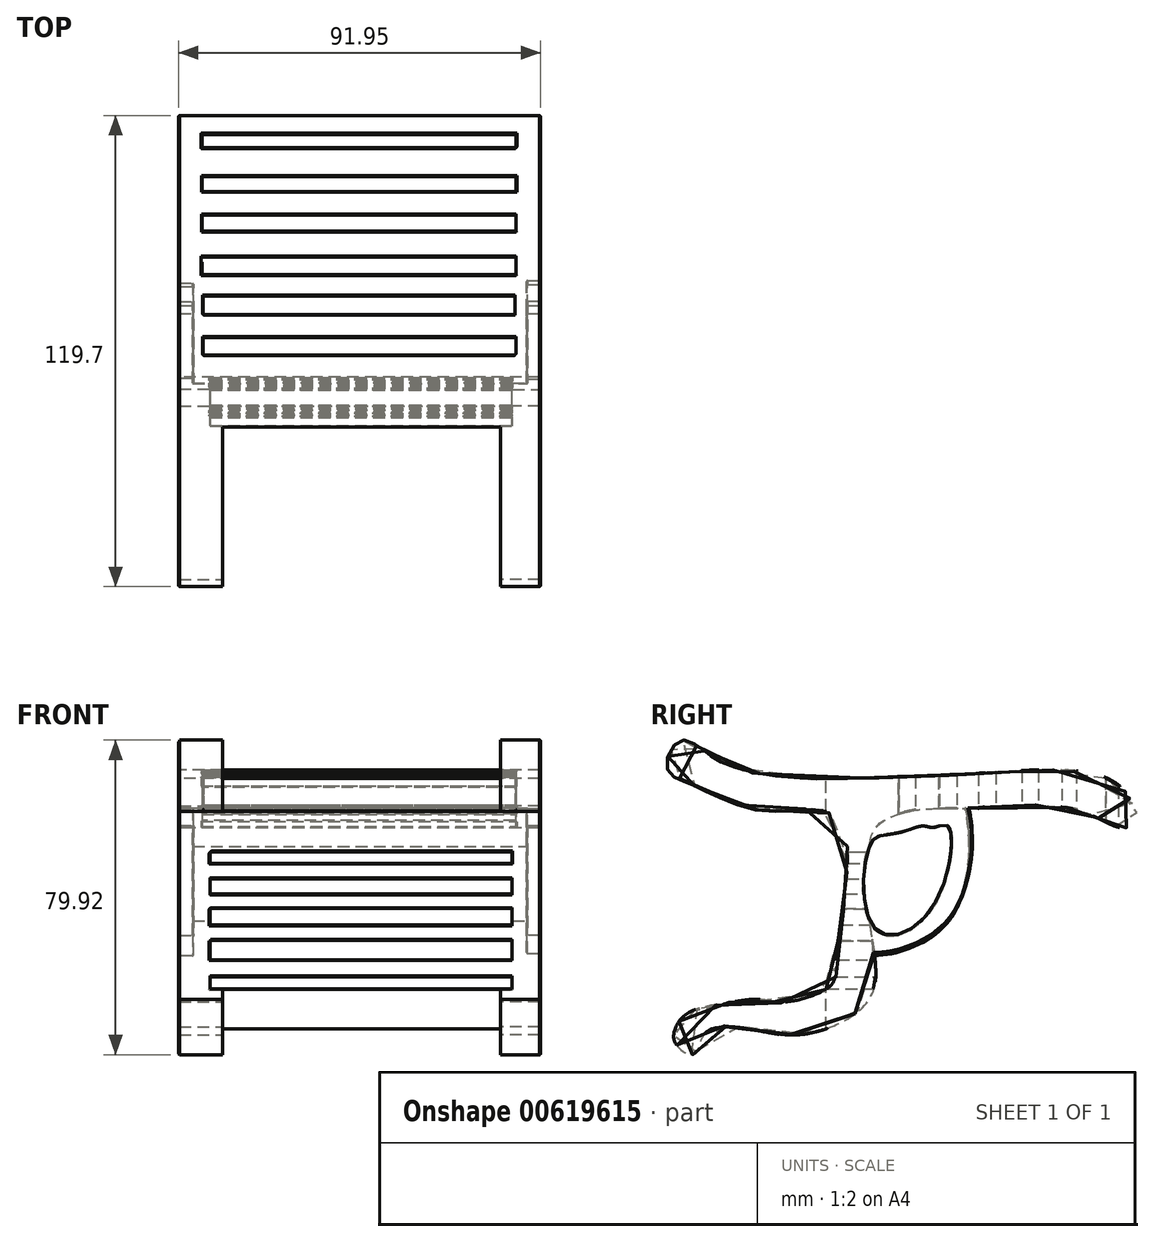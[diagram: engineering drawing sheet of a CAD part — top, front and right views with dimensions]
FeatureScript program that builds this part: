
annotation { "Feature Type Name" : "Feature", "Feature Type Description" : "" }
export const myFeature = defineFeature(function(context is Context, id is Id, definition is map)
    precondition{}
    {
        {
            var Q0;
            Q0=qCreatedBy(makeId("Right.planeOp"),FACE);
            var sketch = newSketch(context, id + "F0", { "sketchPlane" : qUnion([Q0])});
            skFitSpline(sketch, "E0", {"points": [v(46.73, 38) * mm, v(37.67, 44.46) * mm, v(9.54, 44.79) * mm, v(-13.1, 43.82) * mm, v(-44.46, 44.14) * mm, v(-59.01, 48.34) * mm, v(-62.9, 51.25) * mm, v(-68.07, 52.87) * mm, v(-71.3, 46.08) * mm, v(-67.42, 42.84) * mm, v(-61.6, 40.26) * mm, v(-46.4, 35.08) * mm, v(-31.2, 35.08) * mm, v(-26.03, 28.62) * mm, v(-26.35, 11.8) * mm, v(-27.97, 0) * mm, v(-28.94, -8.25) * mm, v(-33.47, -11.48) * mm, v(-41.55, -13.42) * mm, v(-48.02, -12.77) * mm, v(-54.49, -13.42) * mm, v(-64.83, -15.68) * mm, v(-68.71, -19.24) * mm, v(-69.04, -24.1) * mm, v(-64.19, -26.68) * mm, v(-61.92, -21.83) * mm, v(-53.2, -19.89) * mm, v(-40.26, -21.83) * mm, v(-27.65, -18.92) * mm, v(-18.92, -10.83) * mm, v(-19.56, 5.98) * mm, v(-19.89, 25.7) * mm, v(-17.3, 31.85) * mm, v(-7.28, 35.4) * mm, v(5.98, 35.73) * mm, v(32.82, 35.4) * mm, v(43.82, 30.88) * mm, v(48.02, 32.17) * mm, v(46.73, 38) * mm]});
            skSolve(sketch);
        }
        {
            var Q0;
            Q0=makeQuery(id+"F0.imprint","IMPRINT",FACE,{"disambiguationData":[TD([[makeQuery(id+"F0.imprint","IMPRINT",EDGE,{"derivedFrom":sQuery(id+"F0.wireOp",EDGE,"E0")}),1.0]])]});
            extrude(context, id + "F1", {"entities" : qUnion([Q0]), "oppositeDirection" : true, "depth" : 91.95 * mm, "offsetDistance" : 25.4 * mm});
        }
        {
            var Q0;
            Q0=qCreatedBy(makeId("Top.planeOp"),FACE);
            var sketch = newSketch(context, id + "F2", { "sketchPlane" : qUnion([Q0])});
            skLineSegment(sketch, "E1.bottom", {"start": v(-6.18, 43.47) * mm, "end": v(-85.94, 43.47) * mm});
            skLineSegment(sketch, "E1.top", {"start": v(-6.18, 40.12) * mm, "end": v(-85.94, 40.12) * mm});
            skLineSegment(sketch, "E1.left", {"start": v(-6.18, 43.47) * mm, "end": v(-6.18, 40.12) * mm});
            skLineSegment(sketch, "E1.right", {"start": v(-85.94, 43.47) * mm, "end": v(-85.94, 40.12) * mm});
            skLineSegment(sketch, "E2.bottom", {"start": v(-6.18, 32.82) * mm, "end": v(-85.94, 32.82) * mm});
            skLineSegment(sketch, "E2.top", {"start": v(-6.18, 29.04) * mm, "end": v(-85.94, 29.04) * mm});
            skLineSegment(sketch, "E2.left", {"start": v(-6.18, 32.82) * mm, "end": v(-6.18, 29.04) * mm});
            skLineSegment(sketch, "E2.right", {"start": v(-85.94, 32.82) * mm, "end": v(-85.94, 29.04) * mm});
            skLineSegment(sketch, "E3.bottom", {"start": v(-6.18, 23.06) * mm, "end": v(-85.94, 23.06) * mm});
            skLineSegment(sketch, "E3.top", {"start": v(-6.18, 18.94) * mm, "end": v(-85.94, 18.94) * mm});
            skLineSegment(sketch, "E3.left", {"start": v(-6.18, 23.06) * mm, "end": v(-6.18, 18.94) * mm});
            skLineSegment(sketch, "E3.right", {"start": v(-85.94, 23.06) * mm, "end": v(-85.94, 18.94) * mm});
            skLineSegment(sketch, "E4.bottom", {"start": v(-6.18, 12.38) * mm, "end": v(-85.94, 12.38) * mm});
            skLineSegment(sketch, "E4.top", {"start": v(-6.18, 7.9) * mm, "end": v(-85.94, 7.9) * mm});
            skLineSegment(sketch, "E4.left", {"start": v(-6.18, 12.38) * mm, "end": v(-6.18, 7.9) * mm});
            skLineSegment(sketch, "E4.right", {"start": v(-85.94, 12.38) * mm, "end": v(-85.94, 7.9) * mm});
            skLineSegment(sketch, "E5.left", {"start": v(-6.18, 0) * mm, "end": v(-6.18, -5.36) * mm});
            skLineSegment(sketch, "E5.right", {"start": v(-85.94, 0) * mm, "end": v(-85.94, -5.36) * mm});
            skSolve(sketch);
        }
        {
            var Q0;
            Q0 = qSketchRegion(id + "F2", true);
            extrude(context, id + "F3", {"entities" : qUnion([Q0]), "operationType" : NewBodyOperationType.REMOVE, "depth" : 122.68 * mm, "offsetDistance" : 25.4 * mm});
        }
        {
            var Q0;
            Q0=qCreatedBy(makeId("Top.planeOp"),FACE);
            var sketch = newSketch(context, id + "F4", { "sketchPlane" : qUnion([Q0])});
            skLineSegment(sketch, "E6.bottom", {"start": v(-10.2, -30.88) * mm, "end": v(-80.78, -30.88) * mm});
            skLineSegment(sketch, "E6.top", {"start": v(-10.2, -74.25) * mm, "end": v(-80.78, -74.25) * mm});
            skLineSegment(sketch, "E6.left", {"start": v(-10.2, -30.88) * mm, "end": v(-10.2, -74.25) * mm});
            skLineSegment(sketch, "E6.right", {"start": v(-80.78, -30.88) * mm, "end": v(-80.78, -74.25) * mm});
            skSolve(sketch);
        }
        {
            var Q0;
            Q0=makeQuery(id+"F4.imprint","IMPRINT",FACE,{"disambiguationData":[TD([[makeQuery(id+"F4.imprint","IMPRINT",EDGE,{"derivedFrom":sQuery(id+"F4.wireOp",EDGE,"E6.bottom")}),1.0]])]});
            extrude(context, id + "F5", {"entities" : qUnion([Q0]), "operationType" : NewBodyOperationType.REMOVE, "oppositeDirection" : true, "depth" : 64 * mm, "offsetDistance" : 25.4 * mm, "hasSecondDirection" : true, "secondDirectionOppositeDirection" : false, "secondDirectionDepth" : 97.28 * mm});
        }
        {
            var Q0;
            Q0=qCreatedBy(makeId("Front.planeOp"),FACE);
            var sketch = newSketch(context, id + "F6", { "sketchPlane" : qUnion([Q0])});
            skLineSegment(sketch, "E7.bottom", {"start": v(-7.26, 24.75) * mm, "end": v(-83.96, 24.75) * mm});
            skLineSegment(sketch, "E7.top", {"start": v(-7.26, 21.8) * mm, "end": v(-83.96, 21.8) * mm});
            skLineSegment(sketch, "E7.left", {"start": v(-7.26, 24.75) * mm, "end": v(-7.26, 21.8) * mm});
            skLineSegment(sketch, "E7.right", {"start": v(-83.96, 24.75) * mm, "end": v(-83.96, 21.8) * mm});
            skLineSegment(sketch, "E8.bottom", {"start": v(-7.26, 17.89) * mm, "end": v(-83.96, 17.89) * mm});
            skLineSegment(sketch, "E8.top", {"start": v(-7.26, 13.97) * mm, "end": v(-83.96, 13.97) * mm});
            skLineSegment(sketch, "E8.left", {"start": v(-7.26, 17.89) * mm, "end": v(-7.26, 13.97) * mm});
            skLineSegment(sketch, "E8.right", {"start": v(-83.96, 17.89) * mm, "end": v(-83.96, 13.97) * mm});
            skLineSegment(sketch, "E9.bottom", {"start": v(-7.26, 10.3) * mm, "end": v(-83.96, 10.3) * mm});
            skLineSegment(sketch, "E9.top", {"start": v(-7.26, 6.13) * mm, "end": v(-83.96, 6.13) * mm});
            skLineSegment(sketch, "E9.left", {"start": v(-7.26, 10.3) * mm, "end": v(-7.26, 6.13) * mm});
            skLineSegment(sketch, "E9.right", {"start": v(-83.96, 10.3) * mm, "end": v(-83.96, 6.13) * mm});
            skLineSegment(sketch, "E10.bottom", {"start": v(-7.26, 2.2) * mm, "end": v(-83.96, 2.2) * mm});
            skLineSegment(sketch, "E10.top", {"start": v(-7.26, -2.7) * mm, "end": v(-83.96, -2.7) * mm});
            skLineSegment(sketch, "E10.left", {"start": v(-7.26, 2.2) * mm, "end": v(-7.26, -2.7) * mm});
            skLineSegment(sketch, "E10.right", {"start": v(-83.96, 2.2) * mm, "end": v(-83.96, -2.7) * mm});
            skLineSegment(sketch, "E11.bottom", {"start": v(-7.26, -7.1) * mm, "end": v(-83.96, -7.1) * mm});
            skLineSegment(sketch, "E11.top", {"start": v(-7.26, -10.05) * mm, "end": v(-83.96, -10.05) * mm});
            skLineSegment(sketch, "E11.left", {"start": v(-7.26, -7.1) * mm, "end": v(-7.26, -10.05) * mm});
            skLineSegment(sketch, "E11.right", {"start": v(-83.96, -7.1) * mm, "end": v(-83.96, -10.05) * mm});
            skSolve(sketch);
        }
        {
            var Q0;
            Q0=makeQuery(id+"F6.imprint","IMPRINT",FACE,{"disambiguationData":[TD([[makeQuery(id+"F6.imprint","IMPRINT",EDGE,{"derivedFrom":sQuery(id+"F6.wireOp",EDGE,"E8.bottom")}),1.0]])]});
            var Q1;
            Q1=makeQuery(id+"F6.imprint","IMPRINT",FACE,{"disambiguationData":[TD([[makeQuery(id+"F6.imprint","IMPRINT",EDGE,{"derivedFrom":sQuery(id+"F6.wireOp",EDGE,"E9.bottom")}),1.0]])]});
            var Q2;
            Q2=makeQuery(id+"F6.imprint","IMPRINT",FACE,{"disambiguationData":[TD([[makeQuery(id+"F6.imprint","IMPRINT",EDGE,{"derivedFrom":sQuery(id+"F6.wireOp",EDGE,"E10.bottom")}),1.0]])]});
            var Q3;
            Q3=makeQuery(id+"F6.imprint","IMPRINT",FACE,{"disambiguationData":[TD([[makeQuery(id+"F6.imprint","IMPRINT",EDGE,{"derivedFrom":sQuery(id+"F6.wireOp",EDGE,"E11.bottom")}),1.0]])]});
            var Q4;
            Q4=makeQuery(id+"F6.imprint","IMPRINT",FACE,{"disambiguationData":[TD([[makeQuery(id+"F6.imprint","IMPRINT",EDGE,{"derivedFrom":sQuery(id+"F6.wireOp",EDGE,"E7.bottom")}),1.0]])]});
            extrude(context, id + "F7", {"entities" : qUnion([Q0, Q1, Q2, Q3, Q4]), "operationType" : NewBodyOperationType.REMOVE, "depth" : 131.83 * mm, "offsetDistance" : 25.4 * mm});
        }
        {
            var Q0;
            Q0=qCreatedBy(makeId("Top.planeOp"),FACE);
            var sketch = newSketch(context, id + "F8", { "sketchPlane" : qUnion([Q0])});
            skLineSegment(sketch, "E12.bottom", {"start": v(-85.68, 2.45) * mm, "end": v(-6.53, 2.45) * mm});
            skLineSegment(sketch, "E12.top", {"start": v(-85.68, -2.2) * mm, "end": v(-6.53, -2.2) * mm});
            skLineSegment(sketch, "E12.left", {"start": v(-85.68, 2.45) * mm, "end": v(-85.68, -2.2) * mm});
            skLineSegment(sketch, "E12.right", {"start": v(-6.53, 2.45) * mm, "end": v(-6.53, -2.2) * mm});
            skLineSegment(sketch, "E13.bottom", {"start": v(-85.68, -8.09) * mm, "end": v(-6.28, -8.09) * mm});
            skLineSegment(sketch, "E13.top", {"start": v(-85.68, -12.5) * mm, "end": v(-6.28, -12.5) * mm});
            skLineSegment(sketch, "E13.left", {"start": v(-85.68, -8.09) * mm, "end": v(-85.68, -12.5) * mm});
            skLineSegment(sketch, "E13.right", {"start": v(-6.28, -8.09) * mm, "end": v(-6.28, -12.5) * mm});
            skSolve(sketch);
        }
        {
            var Q0;
            Q0=makeQuery(id+"F8.imprint","IMPRINT",FACE,{"disambiguationData":[TD([[makeQuery(id+"F8.imprint","IMPRINT",EDGE,{"derivedFrom":sQuery(id+"F8.wireOp",EDGE,"E13.bottom")}),-1.0]])]});
            var Q1;
            Q1=makeQuery(id+"F8.imprint","IMPRINT",FACE,{"disambiguationData":[TD([[makeQuery(id+"F8.imprint","IMPRINT",EDGE,{"derivedFrom":sQuery(id+"F8.wireOp",EDGE,"E12.bottom")}),-1.0]])]});
            extrude(context, id + "F9", {"entities" : qUnion([Q0, Q1]), "operationType" : NewBodyOperationType.REMOVE, "depth" : 137.92 * mm, "offsetDistance" : 25.4 * mm});
        }
        {
            var Q0;
            Q0=qCreatedBy(makeId("Right.planeOp"),FACE);
            var sketch = newSketch(context, id + "F10", { "sketchPlane" : qUnion([Q0])});
            skFitSpline(sketch, "E14", {"points": [v(3.68, 39.62) * mm, v(0, 7.15) * mm, v(-23.77, 0) * mm, v(-24.33, 3.77) * mm, v(-24.45, 7.59) * mm, v(-24.54, 14.74) * mm, v(-23.4, 26.35) * mm, v(-21.86, 33.21) * mm, v(-13.38, 37.47) * mm, v(-2.7, 40.33) * mm, v(3.68, 39.62) * mm]});
            skSolve(sketch);
        }
        {
            var Q0;
            Q0=qCreatedBy(makeId("Right.planeOp"),FACE);
            cPlane(context, id + "F11", {"entities" : qUnion([Q0]), "cplaneType" : CPlaneType.OFFSET, "offset" : 91.95 * mm, "oppositeDirection" : true, "width" : 152.4 * mm, "height" : 152.4 * mm});
        }
        {
            var Q0;
            Q0=qCreatedBy(id+"F11.planeOp",FACE);
            var sketch = newSketch(context, id + "F12", { "sketchPlane" : qUnion([Q0])});
            skFitSpline(sketch, "E15", {"points": [v(3.68, 39.33) * mm, v(0, 6.74) * mm, v(-25, 0) * mm, v(-24.26, 9.43) * mm, v(-24.26, 17.28) * mm, v(-23.77, 28.06) * mm, v(-21.07, 34.18) * mm, v(-15.2, 37.86) * mm, v(0, 41.78) * mm, v(3.68, 39.33) * mm]});
            skSolve(sketch);
        }
        {
            var Q0;
            Q0=makeQuery(id+"F12.imprint","IMPRINT",FACE,{"disambiguationData":[TD([[makeQuery(id+"F12.imprint","IMPRINT",EDGE,{"derivedFrom":sQuery(id+"F12.wireOp",EDGE,"E15")}),-1.0]])]});
            extrude(context, id + "F13", {"entities" : qUnion([Q0]), "operationType" : NewBodyOperationType.ADD, "depth" : 3.8 * mm, "offsetDistance" : 25.4 * mm});
        }
        {
            var Q0;
            Q0=makeQuery(id+"F10.imprint","IMPRINT",FACE,{"disambiguationData":[TD([[makeQuery(id+"F10.imprint","IMPRINT",EDGE,{"derivedFrom":sQuery(id+"F10.wireOp",EDGE,"E14")}),-1.0]])]});
            extrude(context, id + "F14", {"entities" : qUnion([Q0]), "operationType" : NewBodyOperationType.ADD, "oppositeDirection" : true, "depth" : 3.56 * mm, "offsetDistance" : 25.4 * mm});
        }
        {
            var Q0;
            Q0=qCreatedBy(makeId("Right.planeOp"),FACE);
            var sketch = newSketch(context, id + "F15", { "sketchPlane" : qUnion([Q0])});
            skFitSpline(sketch, "E16", {"points": [v(0, 31.4) * mm, v(-4.05, 10.3) * mm, v(-18.34, 5.12) * mm, v(-19.58, 26.66) * mm, v(-15.73, 29.03) * mm, v(-10.4, 30.08) * mm, v(-6.14, 31.28) * mm, v(-3.42, 30.9) * mm, v(0, 31.4) * mm]});
            skFitSpline(sketch, "E17", {"points": [v(-6.14, 31.28) * mm, v(0, 31.4) * mm], "startDerivative": vector(6.14, 0.12) * mm, "endDerivative": vector(6.14, 0.12) * mm});
            skSolve(sketch);
        }
        {
            var Q0;
            {var subQ0=sQuery(id+"F15.wireOp",EDGE,"E17");var subQ1=sQuery(id+"F15.wireOp",EDGE,"E16");var subQ2=makeQuery(id+"F15.imprint","INTERSECT",VERTEX,{"disambiguationData":[OD(0.0)],"derivedFrom":[subQ1,subQ0]});Q0=makeQuery(id+"F15.imprint","IMPRINT",FACE,{"disambiguationData":[TD([[makeQuery(id+"F15.imprint","IMPRINT",EDGE,{"disambiguationData":[TD([[subQ2,1.0]])],"derivedFrom":subQ1}),-1.0]])]});}
            extrude(context, id + "F16", {"entities" : qUnion([Q0]), "operationType" : NewBodyOperationType.REMOVE, "oppositeDirection" : true, "depth" : 179.58 * mm, "offsetDistance" : 25.4 * mm});
        }
        {
            var Q0;
            Q0=makeQuery(id+"F1.opExtrude","CAP_EDGE",EDGE,{"disambiguationData":[OSD([sQuery(id+"F0.wireOp",EDGE,"E0")])],"isStart":true});
            var Q1;
            Q1=makeQuery(id+"F7.boolean.opBoolean","INTERSECT",EDGE,{"disambiguationData":[OD(1.0)],"derivedFrom":[makeQuery(id+"F1.opExtrude","SWEPT_FACE",FACE,{"disambiguationData":[OSD([sQuery(id+"F0.wireOp",EDGE,"E0")])]}),makeQuery(id+"F7.opExtrude","SWEPT_FACE",FACE,{"disambiguationData":[OSD([sQuery(id+"F6.wireOp",EDGE,"E11.top")])]})]});
            var Q2;
            Q2=makeQuery(id+"F7.boolean.opBoolean","INTERSECT",EDGE,{"disambiguationData":[OD(1.0)],"derivedFrom":[makeQuery(id+"F1.opExtrude","SWEPT_FACE",FACE,{"disambiguationData":[OSD([sQuery(id+"F0.wireOp",EDGE,"E0")])]}),makeQuery(id+"F7.opExtrude","SWEPT_FACE",FACE,{"disambiguationData":[OSD([sQuery(id+"F6.wireOp",EDGE,"E11.bottom")])]})]});
            var Q3;
            Q3=makeQuery(id+"F7.boolean.opBoolean","INTERSECT",EDGE,{"disambiguationData":[OD(1.0)],"derivedFrom":[makeQuery(id+"F1.opExtrude","SWEPT_FACE",FACE,{"disambiguationData":[OSD([sQuery(id+"F0.wireOp",EDGE,"E0")])]}),makeQuery(id+"F7.opExtrude","SWEPT_FACE",FACE,{"disambiguationData":[OSD([sQuery(id+"F6.wireOp",EDGE,"E10.top")])]})]});
            var Q4;
            Q4=makeQuery(id+"F7.boolean.opBoolean","INTERSECT",EDGE,{"disambiguationData":[OD(0.0)],"derivedFrom":[makeQuery(id+"F1.opExtrude","SWEPT_FACE",FACE,{"disambiguationData":[OSD([sQuery(id+"F0.wireOp",EDGE,"E0")])]}),makeQuery(id+"F7.opExtrude","SWEPT_FACE",FACE,{"disambiguationData":[OSD([sQuery(id+"F6.wireOp",EDGE,"E10.bottom")])]})]});
            var Q5;
            Q5=makeQuery(id+"F7.boolean.opBoolean","INTERSECT",EDGE,{"disambiguationData":[OD(1.0)],"derivedFrom":[makeQuery(id+"F1.opExtrude","SWEPT_FACE",FACE,{"disambiguationData":[OSD([sQuery(id+"F0.wireOp",EDGE,"E0")])]}),makeQuery(id+"F7.opExtrude","SWEPT_FACE",FACE,{"disambiguationData":[OSD([sQuery(id+"F6.wireOp",EDGE,"E10.bottom")])]})]});
            var Q6;
            Q6=makeQuery(id+"F7.boolean.opBoolean","INTERSECT",EDGE,{"disambiguationData":[OD(1.0)],"derivedFrom":[makeQuery(id+"F1.opExtrude","SWEPT_FACE",FACE,{"disambiguationData":[OSD([sQuery(id+"F0.wireOp",EDGE,"E0")])]}),makeQuery(id+"F7.opExtrude","SWEPT_FACE",FACE,{"disambiguationData":[OSD([sQuery(id+"F6.wireOp",EDGE,"E9.top")])]})]});
            var Q7;
            Q7=makeQuery(id+"F7.boolean.opBoolean","INTERSECT",EDGE,{"disambiguationData":[OD(0.0)],"derivedFrom":[makeQuery(id+"F1.opExtrude","SWEPT_FACE",FACE,{"disambiguationData":[OSD([sQuery(id+"F0.wireOp",EDGE,"E0")])]}),makeQuery(id+"F7.opExtrude","SWEPT_FACE",FACE,{"disambiguationData":[OSD([sQuery(id+"F6.wireOp",EDGE,"E9.bottom")])]})]});
            var Q8;
            Q8=makeQuery(id+"F16.boolean.opBoolean","INTERSECT",EDGE,{"derivedFrom":[makeQuery(id+"F7.boolean.opBoolean","COPY",FACE,{"derivedFrom":makeQuery(id+"F7.opExtrude","SWEPT_FACE",FACE,{"disambiguationData":[OSD([sQuery(id+"F6.wireOp",EDGE,"E9.bottom")])]})}),makeQuery(id+"F16.opExtrude","SWEPT_FACE",FACE,{"disambiguationData":[OSD([sQuery(id+"F15.wireOp",EDGE,"E16")])]})]});
            var Q9;
            Q9=makeQuery(id+"F16.boolean.opBoolean","INTERSECT",EDGE,{"derivedFrom":[makeQuery(id+"F7.boolean.opBoolean","COPY",FACE,{"derivedFrom":makeQuery(id+"F7.opExtrude","SWEPT_FACE",FACE,{"disambiguationData":[OSD([sQuery(id+"F6.wireOp",EDGE,"E8.top")])]})}),makeQuery(id+"F16.opExtrude","SWEPT_FACE",FACE,{"disambiguationData":[OSD([sQuery(id+"F15.wireOp",EDGE,"E16")])]})]});
            var Q10;
            Q10=makeQuery(id+"F16.boolean.opBoolean","INTERSECT",EDGE,{"derivedFrom":[makeQuery(id+"F7.boolean.opBoolean","COPY",FACE,{"derivedFrom":makeQuery(id+"F7.opExtrude","SWEPT_FACE",FACE,{"disambiguationData":[OSD([sQuery(id+"F6.wireOp",EDGE,"E8.bottom")])]})}),makeQuery(id+"F16.opExtrude","SWEPT_FACE",FACE,{"disambiguationData":[OSD([sQuery(id+"F15.wireOp",EDGE,"E16")])]})]});
            var Q11;
            Q11=makeQuery(id+"F16.boolean.opBoolean","INTERSECT",EDGE,{"derivedFrom":[makeQuery(id+"F7.boolean.opBoolean","COPY",FACE,{"derivedFrom":makeQuery(id+"F7.opExtrude","SWEPT_FACE",FACE,{"disambiguationData":[OSD([sQuery(id+"F6.wireOp",EDGE,"E7.top")])]})}),makeQuery(id+"F16.opExtrude","SWEPT_FACE",FACE,{"disambiguationData":[OSD([sQuery(id+"F15.wireOp",EDGE,"E16")])]})]});
            var Q12;
            Q12=makeQuery(id+"F16.boolean.opBoolean","INTERSECT",EDGE,{"derivedFrom":[makeQuery(id+"F7.boolean.opBoolean","COPY",FACE,{"derivedFrom":makeQuery(id+"F7.opExtrude","SWEPT_FACE",FACE,{"disambiguationData":[OSD([sQuery(id+"F6.wireOp",EDGE,"E7.bottom")])]})}),makeQuery(id+"F16.opExtrude","SWEPT_FACE",FACE,{"disambiguationData":[OSD([sQuery(id+"F15.wireOp",EDGE,"E16")])]})]});
            var Q13;
            Q13=makeQuery(id+"F9.boolean.opBoolean","INTERSECT",EDGE,{"disambiguationData":[OD(0.0)],"derivedFrom":[makeQuery(id+"F1.opExtrude","SWEPT_FACE",FACE,{"disambiguationData":[OSD([sQuery(id+"F0.wireOp",EDGE,"E0")])]}),makeQuery(id+"F9.opExtrude","SWEPT_FACE",FACE,{"disambiguationData":[OSD([sQuery(id+"F8.wireOp",EDGE,"E13.top")])]})]});
            var Q14;
            Q14=makeQuery(id+"F9.boolean.opBoolean","INTERSECT",EDGE,{"disambiguationData":[OD(0.0)],"derivedFrom":[makeQuery(id+"F1.opExtrude","SWEPT_FACE",FACE,{"disambiguationData":[OSD([sQuery(id+"F0.wireOp",EDGE,"E0")])]}),makeQuery(id+"F9.opExtrude","SWEPT_FACE",FACE,{"disambiguationData":[OSD([sQuery(id+"F8.wireOp",EDGE,"E13.bottom")])]})]});
            var Q15;
            Q15=makeQuery(id+"F9.boolean.opBoolean","INTERSECT",EDGE,{"disambiguationData":[OD(0.0)],"derivedFrom":[makeQuery(id+"F1.opExtrude","SWEPT_FACE",FACE,{"disambiguationData":[OSD([sQuery(id+"F0.wireOp",EDGE,"E0")])]}),makeQuery(id+"F9.opExtrude","SWEPT_FACE",FACE,{"disambiguationData":[OSD([sQuery(id+"F8.wireOp",EDGE,"E12.top")])]})]});
            var Q16;
            Q16=makeQuery(id+"F9.boolean.opBoolean","INTERSECT",EDGE,{"disambiguationData":[OD(0.0)],"derivedFrom":[makeQuery(id+"F1.opExtrude","SWEPT_FACE",FACE,{"disambiguationData":[OSD([sQuery(id+"F0.wireOp",EDGE,"E0")])]}),makeQuery(id+"F9.opExtrude","SWEPT_FACE",FACE,{"disambiguationData":[OSD([sQuery(id+"F8.wireOp",EDGE,"E12.bottom")])]})]});
            var Q17;
            Q17=makeQuery(id+"F3.boolean.opBoolean","INTERSECT",EDGE,{"disambiguationData":[OD(0.0)],"derivedFrom":[makeQuery(id+"F1.opExtrude","SWEPT_FACE",FACE,{"disambiguationData":[OSD([sQuery(id+"F0.wireOp",EDGE,"E0")])]}),makeQuery(id+"F3.opExtrude","SWEPT_FACE",FACE,{"disambiguationData":[OSD([sQuery(id+"F2.wireOp",EDGE,"E4.top")])]})]});
            var Q18;
            Q18=makeQuery(id+"F3.boolean.opBoolean","INTERSECT",EDGE,{"disambiguationData":[OD(0.0)],"derivedFrom":[makeQuery(id+"F1.opExtrude","SWEPT_FACE",FACE,{"disambiguationData":[OSD([sQuery(id+"F0.wireOp",EDGE,"E0")])]}),makeQuery(id+"F3.opExtrude","SWEPT_FACE",FACE,{"disambiguationData":[OSD([sQuery(id+"F2.wireOp",EDGE,"E3.top")])]})]});
            var Q19;
            Q19=makeQuery(id+"F3.boolean.opBoolean","INTERSECT",EDGE,{"disambiguationData":[OD(0.0)],"derivedFrom":[makeQuery(id+"F1.opExtrude","SWEPT_FACE",FACE,{"disambiguationData":[OSD([sQuery(id+"F0.wireOp",EDGE,"E0")])]}),makeQuery(id+"F3.opExtrude","SWEPT_FACE",FACE,{"disambiguationData":[OSD([sQuery(id+"F2.wireOp",EDGE,"E3.bottom")])]})]});
            var Q20;
            Q20=makeQuery(id+"F3.boolean.opBoolean","INTERSECT",EDGE,{"disambiguationData":[OD(0.0)],"derivedFrom":[makeQuery(id+"F1.opExtrude","SWEPT_FACE",FACE,{"disambiguationData":[OSD([sQuery(id+"F0.wireOp",EDGE,"E0")])]}),makeQuery(id+"F3.opExtrude","SWEPT_FACE",FACE,{"disambiguationData":[OSD([sQuery(id+"F2.wireOp",EDGE,"E2.top")])]})]});
            var Q21;
            Q21=makeQuery(id+"F3.boolean.opBoolean","INTERSECT",EDGE,{"disambiguationData":[OD(0.0)],"derivedFrom":[makeQuery(id+"F1.opExtrude","SWEPT_FACE",FACE,{"disambiguationData":[OSD([sQuery(id+"F0.wireOp",EDGE,"E0")])]}),makeQuery(id+"F3.opExtrude","SWEPT_FACE",FACE,{"disambiguationData":[OSD([sQuery(id+"F2.wireOp",EDGE,"E2.bottom")])]})]});
            var Q22;
            Q22=makeQuery(id+"F3.boolean.opBoolean","INTERSECT",EDGE,{"disambiguationData":[OD(0.0)],"derivedFrom":[makeQuery(id+"F1.opExtrude","SWEPT_FACE",FACE,{"disambiguationData":[OSD([sQuery(id+"F0.wireOp",EDGE,"E0")])]}),makeQuery(id+"F3.opExtrude","SWEPT_FACE",FACE,{"disambiguationData":[OSD([sQuery(id+"F2.wireOp",EDGE,"E1.top")])]})]});
            var Q23;
            Q23=makeQuery(id+"F3.boolean.opBoolean","INTERSECT",EDGE,{"disambiguationData":[OD(0.0)],"derivedFrom":[makeQuery(id+"F1.opExtrude","SWEPT_FACE",FACE,{"disambiguationData":[OSD([sQuery(id+"F0.wireOp",EDGE,"E0")])]}),makeQuery(id+"F3.opExtrude","SWEPT_FACE",FACE,{"disambiguationData":[OSD([sQuery(id+"F2.wireOp",EDGE,"E1.bottom")])]})]});
            var Q24;
            Q24=makeQuery(id+"F3.boolean.opBoolean","INTERSECT",EDGE,{"disambiguationData":[OD(0.0)],"derivedFrom":[makeQuery(id+"F1.opExtrude","SWEPT_FACE",FACE,{"disambiguationData":[OSD([sQuery(id+"F0.wireOp",EDGE,"E0")])]}),makeQuery(id+"F3.opExtrude","SWEPT_FACE",FACE,{"disambiguationData":[OSD([sQuery(id+"F2.wireOp",EDGE,"E4.bottom")])]})]});
            var Q25;
            Q25=makeQuery(id+"F3.boolean.opBoolean","INTERSECT",EDGE,{"disambiguationData":[OD(0.0)],"derivedFrom":[makeQuery(id+"F1.opExtrude","SWEPT_FACE",FACE,{"disambiguationData":[OSD([sQuery(id+"F0.wireOp",EDGE,"E0")])]}),makeQuery(id+"F3.opExtrude","SWEPT_FACE",FACE,{"disambiguationData":[OSD([sQuery(id+"F2.wireOp",EDGE,"E4.left")])]})]});
            var Q26;
            Q26=makeQuery(id+"F3.boolean.opBoolean","INTERSECT",EDGE,{"disambiguationData":[OD(0.0)],"derivedFrom":[makeQuery(id+"F1.opExtrude","SWEPT_FACE",FACE,{"disambiguationData":[OSD([sQuery(id+"F0.wireOp",EDGE,"E0")])]}),makeQuery(id+"F3.opExtrude","SWEPT_FACE",FACE,{"disambiguationData":[OSD([sQuery(id+"F2.wireOp",EDGE,"E3.left")])]})]});
            var Q27;
            Q27=makeQuery(id+"F3.boolean.opBoolean","INTERSECT",EDGE,{"disambiguationData":[OD(0.0)],"derivedFrom":[makeQuery(id+"F1.opExtrude","SWEPT_FACE",FACE,{"disambiguationData":[OSD([sQuery(id+"F0.wireOp",EDGE,"E0")])]}),makeQuery(id+"F3.opExtrude","SWEPT_FACE",FACE,{"disambiguationData":[OSD([sQuery(id+"F2.wireOp",EDGE,"E2.left")])]})]});
            var Q28;
            Q28=makeQuery(id+"F3.boolean.opBoolean","INTERSECT",EDGE,{"disambiguationData":[OD(0.0)],"derivedFrom":[makeQuery(id+"F1.opExtrude","SWEPT_FACE",FACE,{"disambiguationData":[OSD([sQuery(id+"F0.wireOp",EDGE,"E0")])]}),makeQuery(id+"F3.opExtrude","SWEPT_FACE",FACE,{"disambiguationData":[OSD([sQuery(id+"F2.wireOp",EDGE,"E1.left")])]})]});
            var Q29;
            Q29=makeQuery(id+"F14.opExtrude","CAP_EDGE",EDGE,{"disambiguationData":[OSD([sQuery(id+"F10.wireOp",EDGE,"E14")])],"isStart":true});
            var Q30;
            Q30=makeQuery(id+"F14.opExtrude","CAP_EDGE",EDGE,{"disambiguationData":[OSD([sQuery(id+"F10.wireOp",EDGE,"E14")])],"isStart":false});
            var Q31;
            Q31=makeQuery(id+"F16.boolean.opBoolean","INTERSECT",EDGE,{"disambiguationData":[OD(1.0)],"derivedFrom":[makeQuery(id+"F14.opExtrude","CAP_FACE",FACE,{"disambiguationData":[OSD([sQuery(id+"F10.wireOp",EDGE,"E14")])],"isStart":false}),makeQuery(id+"F16.opExtrude","SWEPT_FACE",FACE,{"disambiguationData":[OSD([sQuery(id+"F15.wireOp",EDGE,"E16")])]})]});
            var Q32;
            Q32=makeQuery(id+"F16.boolean.opBoolean","COPY",EDGE,{"derivedFrom":makeQuery(id+"F16.opExtrude","CAP_EDGE",EDGE,{"disambiguationData":[OSD([sQuery(id+"F15.wireOp",EDGE,"E16")])],"isStart":true})});
            var Q33;
            Q33=makeQuery(id+"F9.boolean.opBoolean","COPY",EDGE,{"derivedFrom":makeQuery(id+"F9.opExtrude","SWEPT_EDGE",EDGE,{"disambiguationData":[OSD([sQuery(id+"F8.wireOp",EDGE,"E13.top"),sQuery(id+"F8.wireOp",EDGE,"E13.right")])]})});
            var Q34;
            Q34=makeQuery(id+"F9.boolean.opBoolean","INTERSECT",EDGE,{"disambiguationData":[OD(0.0)],"derivedFrom":[makeQuery(id+"F1.opExtrude","SWEPT_FACE",FACE,{"disambiguationData":[OSD([sQuery(id+"F0.wireOp",EDGE,"E0")])]}),makeQuery(id+"F9.opExtrude","SWEPT_FACE",FACE,{"disambiguationData":[OSD([sQuery(id+"F8.wireOp",EDGE,"E12.right")])]})]});
            var Q35;
            Q35=makeQuery(id+"F16.boolean.opBoolean","INTERSECT",EDGE,{"disambiguationData":[OD(0.0)],"derivedFrom":[makeQuery(id+"F14.opExtrude","CAP_FACE",FACE,{"disambiguationData":[OSD([sQuery(id+"F10.wireOp",EDGE,"E14")])],"isStart":false}),makeQuery(id+"F16.opExtrude","SWEPT_FACE",FACE,{"disambiguationData":[OSD([sQuery(id+"F15.wireOp",EDGE,"E16")])]})]});
            var Q36;
            Q36=makeQuery(id+"F16.boolean.opBoolean","INTERSECT",EDGE,{"derivedFrom":[makeQuery(id+"F7.boolean.opBoolean","COPY",FACE,{"derivedFrom":makeQuery(id+"F7.opExtrude","SWEPT_FACE",FACE,{"disambiguationData":[OSD([sQuery(id+"F6.wireOp",EDGE,"E7.left")])]})}),makeQuery(id+"F16.opExtrude","SWEPT_FACE",FACE,{"disambiguationData":[OSD([sQuery(id+"F15.wireOp",EDGE,"E16")])]})]});
            var Q37;
            Q37=makeQuery(id+"F7.boolean.opBoolean","INTERSECT",EDGE,{"disambiguationData":[OD(0.0)],"derivedFrom":[makeQuery(id+"F1.opExtrude","SWEPT_FACE",FACE,{"disambiguationData":[OSD([sQuery(id+"F0.wireOp",EDGE,"E0")])]}),makeQuery(id+"F7.opExtrude","SWEPT_FACE",FACE,{"disambiguationData":[OSD([sQuery(id+"F6.wireOp",EDGE,"E7.left")])]})]});
            var Q38;
            Q38=makeQuery(id+"F16.boolean.opBoolean","INTERSECT",EDGE,{"derivedFrom":[makeQuery(id+"F7.boolean.opBoolean","COPY",FACE,{"derivedFrom":makeQuery(id+"F7.opExtrude","SWEPT_FACE",FACE,{"disambiguationData":[OSD([sQuery(id+"F6.wireOp",EDGE,"E8.left")])]})}),makeQuery(id+"F16.opExtrude","SWEPT_FACE",FACE,{"disambiguationData":[OSD([sQuery(id+"F15.wireOp",EDGE,"E16")])]})]});
            var Q39;
            Q39=makeQuery(id+"F16.boolean.opBoolean","INTERSECT",EDGE,{"derivedFrom":[makeQuery(id+"F7.boolean.opBoolean","COPY",FACE,{"derivedFrom":makeQuery(id+"F7.opExtrude","SWEPT_FACE",FACE,{"disambiguationData":[OSD([sQuery(id+"F6.wireOp",EDGE,"E9.left")])]})}),makeQuery(id+"F16.opExtrude","SWEPT_FACE",FACE,{"disambiguationData":[OSD([sQuery(id+"F15.wireOp",EDGE,"E16")])]})]});
            var Q40;
            Q40=makeQuery(id+"F7.boolean.opBoolean","INTERSECT",EDGE,{"disambiguationData":[OD(1.0)],"derivedFrom":[makeQuery(id+"F1.opExtrude","SWEPT_FACE",FACE,{"disambiguationData":[OSD([sQuery(id+"F0.wireOp",EDGE,"E0")])]}),makeQuery(id+"F7.opExtrude","SWEPT_FACE",FACE,{"disambiguationData":[OSD([sQuery(id+"F6.wireOp",EDGE,"E11.left")])]})]});
            var Q41;
            Q41=makeQuery(id+"F7.boolean.opBoolean","INTERSECT",EDGE,{"disambiguationData":[OD(1.0)],"derivedFrom":[makeQuery(id+"F1.opExtrude","SWEPT_FACE",FACE,{"disambiguationData":[OSD([sQuery(id+"F0.wireOp",EDGE,"E0")])]}),makeQuery(id+"F7.opExtrude","SWEPT_FACE",FACE,{"disambiguationData":[OSD([sQuery(id+"F6.wireOp",EDGE,"E10.left")])]})]});
            var Q42;
            Q42=makeQuery(id+"F1.opExtrude","CAP_EDGE",EDGE,{"disambiguationData":[OSD([sQuery(id+"F0.wireOp",EDGE,"E0")])],"isStart":false});
            var Q43;
            Q43=makeQuery(id+"F13.opExtrude","CAP_EDGE",EDGE,{"disambiguationData":[OSD([sQuery(id+"F12.wireOp",EDGE,"E15")])],"isStart":true});
            var Q44;
            Q44=makeQuery(id+"F13.opExtrude","CAP_EDGE",EDGE,{"disambiguationData":[OSD([sQuery(id+"F12.wireOp",EDGE,"E15")])],"isStart":false});
            var Q45;
            Q45=makeQuery(id+"F16.boolean.opBoolean","INTERSECT",EDGE,{"disambiguationData":[OD(1.0)],"derivedFrom":[makeQuery(id+"F13.opExtrude","CAP_FACE",FACE,{"disambiguationData":[OSD([sQuery(id+"F12.wireOp",EDGE,"E15")])],"isStart":false}),makeQuery(id+"F16.opExtrude","SWEPT_FACE",FACE,{"disambiguationData":[OSD([sQuery(id+"F15.wireOp",EDGE,"E16")])]})]});
            var Q46;
            Q46=makeQuery(id+"F16.boolean.opBoolean","INTERSECT",EDGE,{"derivedFrom":[makeQuery(id+"F13.boolean.opBoolean","MERGE",FACE,{"derivedFrom":[makeQuery(id+"F1.opExtrude","CAP_FACE",FACE,{"disambiguationData":[OSD([sQuery(id+"F0.wireOp",EDGE,"E0")])],"isStart":false}),makeQuery(id+"F13.opExtrude","CAP_FACE",FACE,{"disambiguationData":[OSD([sQuery(id+"F12.wireOp",EDGE,"E15")])],"isStart":true})]}),makeQuery(id+"F16.opExtrude","SWEPT_FACE",FACE,{"disambiguationData":[OSD([sQuery(id+"F15.wireOp",EDGE,"E16")])]})]});
            var Q47;
            Q47=makeQuery(id+"F7.boolean.opBoolean","INTERSECT",EDGE,{"disambiguationData":[OD(1.0)],"derivedFrom":[makeQuery(id+"F1.opExtrude","SWEPT_FACE",FACE,{"disambiguationData":[OSD([sQuery(id+"F0.wireOp",EDGE,"E0")])]}),makeQuery(id+"F7.opExtrude","SWEPT_FACE",FACE,{"disambiguationData":[OSD([sQuery(id+"F6.wireOp",EDGE,"E11.right")])]})]});
            var Q48;
            Q48=makeQuery(id+"F7.boolean.opBoolean","COPY",EDGE,{"derivedFrom":makeQuery(id+"F7.opExtrude","SWEPT_EDGE",EDGE,{"disambiguationData":[OSD([sQuery(id+"F6.wireOp",EDGE,"E10.bottom"),sQuery(id+"F6.wireOp",EDGE,"E10.right")])]})});
            var Q49;
            Q49=makeQuery(id+"F16.boolean.opBoolean","INTERSECT",EDGE,{"derivedFrom":[makeQuery(id+"F7.boolean.opBoolean","COPY",FACE,{"derivedFrom":makeQuery(id+"F7.opExtrude","SWEPT_FACE",FACE,{"disambiguationData":[OSD([sQuery(id+"F6.wireOp",EDGE,"E9.right")])]})}),makeQuery(id+"F16.opExtrude","SWEPT_FACE",FACE,{"disambiguationData":[OSD([sQuery(id+"F15.wireOp",EDGE,"E16")])]})]});
            var Q50;
            Q50=makeQuery(id+"F16.boolean.opBoolean","INTERSECT",EDGE,{"derivedFrom":[makeQuery(id+"F7.boolean.opBoolean","COPY",FACE,{"derivedFrom":makeQuery(id+"F7.opExtrude","SWEPT_FACE",FACE,{"disambiguationData":[OSD([sQuery(id+"F6.wireOp",EDGE,"E8.right")])]})}),makeQuery(id+"F16.opExtrude","SWEPT_FACE",FACE,{"disambiguationData":[OSD([sQuery(id+"F15.wireOp",EDGE,"E16")])]})]});
            var Q51;
            Q51=makeQuery(id+"F7.boolean.opBoolean","COPY",EDGE,{"derivedFrom":makeQuery(id+"F7.opExtrude","SWEPT_EDGE",EDGE,{"disambiguationData":[OSD([sQuery(id+"F6.wireOp",EDGE,"E7.bottom"),sQuery(id+"F6.wireOp",EDGE,"E7.right")])]})});
            var Q52;
            Q52=makeQuery(id+"F7.boolean.opBoolean","COPY",EDGE,{"derivedFrom":makeQuery(id+"F7.opExtrude","SWEPT_EDGE",EDGE,{"disambiguationData":[OSD([sQuery(id+"F6.wireOp",EDGE,"E9.bottom"),sQuery(id+"F6.wireOp",EDGE,"E9.right")])]})});
            var Q53;
            Q53=makeQuery(id+"F3.boolean.opBoolean","INTERSECT",EDGE,{"disambiguationData":[OD(0.0)],"derivedFrom":[makeQuery(id+"F1.opExtrude","SWEPT_FACE",FACE,{"disambiguationData":[OSD([sQuery(id+"F0.wireOp",EDGE,"E0")])]}),makeQuery(id+"F3.opExtrude","SWEPT_FACE",FACE,{"disambiguationData":[OSD([sQuery(id+"F2.wireOp",EDGE,"E1.right")])]})]});
            var Q54;
            Q54=makeQuery(id+"F3.boolean.opBoolean","INTERSECT",EDGE,{"disambiguationData":[OD(0.0)],"derivedFrom":[makeQuery(id+"F1.opExtrude","SWEPT_FACE",FACE,{"disambiguationData":[OSD([sQuery(id+"F0.wireOp",EDGE,"E0")])]}),makeQuery(id+"F3.opExtrude","SWEPT_FACE",FACE,{"disambiguationData":[OSD([sQuery(id+"F2.wireOp",EDGE,"E2.right")])]})]});
            var Q55;
            Q55=makeQuery(id+"F3.boolean.opBoolean","INTERSECT",EDGE,{"disambiguationData":[OD(0.0)],"derivedFrom":[makeQuery(id+"F1.opExtrude","SWEPT_FACE",FACE,{"disambiguationData":[OSD([sQuery(id+"F0.wireOp",EDGE,"E0")])]}),makeQuery(id+"F3.opExtrude","SWEPT_FACE",FACE,{"disambiguationData":[OSD([sQuery(id+"F2.wireOp",EDGE,"E3.right")])]})]});
            var Q56;
            Q56=makeQuery(id+"F3.boolean.opBoolean","INTERSECT",EDGE,{"disambiguationData":[OD(1.0)],"derivedFrom":[makeQuery(id+"F1.opExtrude","SWEPT_FACE",FACE,{"disambiguationData":[OSD([sQuery(id+"F0.wireOp",EDGE,"E0")])]}),makeQuery(id+"F3.opExtrude","SWEPT_FACE",FACE,{"disambiguationData":[OSD([sQuery(id+"F2.wireOp",EDGE,"E4.right")])]})]});
            var Q57;
            Q57=makeQuery(id+"F9.boolean.opBoolean","INTERSECT",EDGE,{"disambiguationData":[OD(0.0)],"derivedFrom":[makeQuery(id+"F1.opExtrude","SWEPT_FACE",FACE,{"disambiguationData":[OSD([sQuery(id+"F0.wireOp",EDGE,"E0")])]}),makeQuery(id+"F9.opExtrude","SWEPT_FACE",FACE,{"disambiguationData":[OSD([sQuery(id+"F8.wireOp",EDGE,"E12.left")])]})]});
            var Q58;
            Q58=makeQuery(id+"F9.boolean.opBoolean","INTERSECT",EDGE,{"disambiguationData":[OD(0.0)],"derivedFrom":[makeQuery(id+"F1.opExtrude","SWEPT_FACE",FACE,{"disambiguationData":[OSD([sQuery(id+"F0.wireOp",EDGE,"E0")])]}),makeQuery(id+"F9.opExtrude","SWEPT_FACE",FACE,{"disambiguationData":[OSD([sQuery(id+"F8.wireOp",EDGE,"E13.left")])]})]});
            var Q59;
            Q59=makeQuery(id+"F3.boolean.opBoolean","INTERSECT",EDGE,{"disambiguationData":[OD(0.0)],"derivedFrom":[makeQuery(id+"F1.opExtrude","SWEPT_FACE",FACE,{"disambiguationData":[OSD([sQuery(id+"F0.wireOp",EDGE,"E0")])]}),makeQuery(id+"F3.opExtrude","SWEPT_FACE",FACE,{"disambiguationData":[OSD([sQuery(id+"F2.wireOp",EDGE,"E4.right")])]})]});
            var Q60;
            Q60=makeQuery(id+"F3.boolean.opBoolean","INTERSECT",EDGE,{"disambiguationData":[OD(1.0)],"derivedFrom":[makeQuery(id+"F1.opExtrude","SWEPT_FACE",FACE,{"disambiguationData":[OSD([sQuery(id+"F0.wireOp",EDGE,"E0")])]}),makeQuery(id+"F3.opExtrude","SWEPT_FACE",FACE,{"disambiguationData":[OSD([sQuery(id+"F2.wireOp",EDGE,"E1.bottom")])]})]});
            var Q61;
            Q61=makeQuery(id+"F3.boolean.opBoolean","INTERSECT",EDGE,{"disambiguationData":[OD(1.0)],"derivedFrom":[makeQuery(id+"F1.opExtrude","SWEPT_FACE",FACE,{"disambiguationData":[OSD([sQuery(id+"F0.wireOp",EDGE,"E0")])]}),makeQuery(id+"F3.opExtrude","SWEPT_FACE",FACE,{"disambiguationData":[OSD([sQuery(id+"F2.wireOp",EDGE,"E1.left")])]})]});
            var Q62;
            Q62=makeQuery(id+"F3.boolean.opBoolean","INTERSECT",EDGE,{"disambiguationData":[OD(1.0)],"derivedFrom":[makeQuery(id+"F1.opExtrude","SWEPT_FACE",FACE,{"disambiguationData":[OSD([sQuery(id+"F0.wireOp",EDGE,"E0")])]}),makeQuery(id+"F3.opExtrude","SWEPT_FACE",FACE,{"disambiguationData":[OSD([sQuery(id+"F2.wireOp",EDGE,"E1.right")])]})]});
            var Q63;
            Q63=makeQuery(id+"F3.boolean.opBoolean","INTERSECT",EDGE,{"disambiguationData":[OD(1.0)],"derivedFrom":[makeQuery(id+"F1.opExtrude","SWEPT_FACE",FACE,{"disambiguationData":[OSD([sQuery(id+"F0.wireOp",EDGE,"E0")])]}),makeQuery(id+"F3.opExtrude","SWEPT_FACE",FACE,{"disambiguationData":[OSD([sQuery(id+"F2.wireOp",EDGE,"E1.top")])]})]});
            var Q64;
            Q64=makeQuery(id+"F3.boolean.opBoolean","COPY",EDGE,{"derivedFrom":makeQuery(id+"F3.opExtrude","SWEPT_EDGE",EDGE,{"disambiguationData":[OSD([sQuery(id+"F2.wireOp",EDGE,"E1.top"),sQuery(id+"F2.wireOp",EDGE,"E1.left")])]})});
            var Q65;
            Q65=makeQuery(id+"F3.boolean.opBoolean","INTERSECT",EDGE,{"disambiguationData":[OD(1.0)],"derivedFrom":[makeQuery(id+"F1.opExtrude","SWEPT_FACE",FACE,{"disambiguationData":[OSD([sQuery(id+"F0.wireOp",EDGE,"E0")])]}),makeQuery(id+"F3.opExtrude","SWEPT_FACE",FACE,{"disambiguationData":[OSD([sQuery(id+"F2.wireOp",EDGE,"E2.left")])]})]});
            var Q66;
            Q66=makeQuery(id+"F3.boolean.opBoolean","INTERSECT",EDGE,{"disambiguationData":[OD(1.0)],"derivedFrom":[makeQuery(id+"F1.opExtrude","SWEPT_FACE",FACE,{"disambiguationData":[OSD([sQuery(id+"F0.wireOp",EDGE,"E0")])]}),makeQuery(id+"F3.opExtrude","SWEPT_FACE",FACE,{"disambiguationData":[OSD([sQuery(id+"F2.wireOp",EDGE,"E2.top")])]})]});
            var Q67;
            Q67=makeQuery(id+"F3.boolean.opBoolean","INTERSECT",EDGE,{"disambiguationData":[OD(1.0)],"derivedFrom":[makeQuery(id+"F1.opExtrude","SWEPT_FACE",FACE,{"disambiguationData":[OSD([sQuery(id+"F0.wireOp",EDGE,"E0")])]}),makeQuery(id+"F3.opExtrude","SWEPT_FACE",FACE,{"disambiguationData":[OSD([sQuery(id+"F2.wireOp",EDGE,"E3.top")])]})]});
            var Q68;
            Q68=makeQuery(id+"F3.boolean.opBoolean","INTERSECT",EDGE,{"disambiguationData":[OD(1.0)],"derivedFrom":[makeQuery(id+"F1.opExtrude","SWEPT_FACE",FACE,{"disambiguationData":[OSD([sQuery(id+"F0.wireOp",EDGE,"E0")])]}),makeQuery(id+"F3.opExtrude","SWEPT_FACE",FACE,{"disambiguationData":[OSD([sQuery(id+"F2.wireOp",EDGE,"E3.bottom")])]})]});
            chamfer(context, id + "F17", {"entities" : qUnion([Q0, Q1, Q2, Q3, Q4, Q5, Q6, Q7, Q8, Q9, Q10, Q11, Q12, Q13, Q14, Q15, Q16, Q17, Q18, Q19, Q20, Q21, Q22, Q23, Q24, Q25, Q26, Q27, Q28, Q29, Q30, Q31, Q32, Q33, Q34, Q35, Q36, Q37, Q38, Q39, Q40, Q41, Q42, Q43, Q44, Q45, Q46, Q47, Q48, Q49, Q50, Q51, Q52, Q53, Q54, Q55, Q56, Q57, Q58, Q59, Q60, Q61, Q62, Q63, Q64, Q65, Q66, Q67, Q68]), "width" : 0.2 * mm, "tangentPropagation" : true});
        }
        {
            var Q0;
            {var subQ0=makeQuery(id+"F1.opExtrude","SWEPT_FACE",FACE,{"disambiguationData":[OSD([sQuery(id+"F0.wireOp",EDGE,"E0")])]});Q0=makeQuery(id+"F17.opChamfer","BLEND_EDGE",EDGE,{"blendedFrom":[makeQuery(id+"F3.boolean.opBoolean","INTERSECT",EDGE,{"disambiguationData":[OD(1.0)],"derivedFrom":[subQ0,makeQuery(id+"F3.opExtrude","SWEPT_FACE",FACE,{"disambiguationData":[OSD([sQuery(id+"F2.wireOp",EDGE,"E1.top")])]})]}),subQ0],"blendedInto":[subQ0]});}
            var Q1;
            Q1=makeQuery(id+"F3.boolean.opBoolean","INTERSECT",EDGE,{"disambiguationData":[OD(1.0)],"derivedFrom":[makeQuery(id+"F1.opExtrude","SWEPT_FACE",FACE,{"disambiguationData":[OSD([sQuery(id+"F0.wireOp",EDGE,"E0")])]}),makeQuery(id+"F3.opExtrude","SWEPT_FACE",FACE,{"disambiguationData":[OSD([sQuery(id+"F2.wireOp",EDGE,"E4.top")])]})]});
            var Q2;
            Q2=makeQuery(id+"F9.boolean.opBoolean","INTERSECT",EDGE,{"disambiguationData":[OD(1.0)],"derivedFrom":[makeQuery(id+"F1.opExtrude","SWEPT_FACE",FACE,{"disambiguationData":[OSD([sQuery(id+"F0.wireOp",EDGE,"E0")])]}),makeQuery(id+"F9.opExtrude","SWEPT_FACE",FACE,{"disambiguationData":[OSD([sQuery(id+"F8.wireOp",EDGE,"E12.top")])]})]});
            var Q3;
            Q3=makeQuery(id+"F9.boolean.opBoolean","INTERSECT",EDGE,{"disambiguationData":[OD(1.0)],"derivedFrom":[makeQuery(id+"F1.opExtrude","SWEPT_FACE",FACE,{"disambiguationData":[OSD([sQuery(id+"F0.wireOp",EDGE,"E0")])]}),makeQuery(id+"F9.opExtrude","SWEPT_FACE",FACE,{"disambiguationData":[OSD([sQuery(id+"F8.wireOp",EDGE,"E13.top")])]})]});
            var Q4;
            Q4=makeQuery(id+"F9.boolean.opBoolean","INTERSECT",EDGE,{"disambiguationData":[OD(1.0)],"derivedFrom":[makeQuery(id+"F1.opExtrude","SWEPT_FACE",FACE,{"disambiguationData":[OSD([sQuery(id+"F0.wireOp",EDGE,"E0")])]}),makeQuery(id+"F9.opExtrude","SWEPT_FACE",FACE,{"disambiguationData":[OSD([sQuery(id+"F8.wireOp",EDGE,"E13.bottom")])]})]});
            var Q5;
            Q5=makeQuery(id+"F9.boolean.opBoolean","INTERSECT",EDGE,{"disambiguationData":[OD(1.0)],"derivedFrom":[makeQuery(id+"F1.opExtrude","SWEPT_FACE",FACE,{"disambiguationData":[OSD([sQuery(id+"F0.wireOp",EDGE,"E0")])]}),makeQuery(id+"F9.opExtrude","SWEPT_FACE",FACE,{"disambiguationData":[OSD([sQuery(id+"F8.wireOp",EDGE,"E12.bottom")])]})]});
            var Q6;
            Q6=makeQuery(id+"F3.boolean.opBoolean","INTERSECT",EDGE,{"disambiguationData":[OD(1.0)],"derivedFrom":[makeQuery(id+"F1.opExtrude","SWEPT_FACE",FACE,{"disambiguationData":[OSD([sQuery(id+"F0.wireOp",EDGE,"E0")])]}),makeQuery(id+"F3.opExtrude","SWEPT_FACE",FACE,{"disambiguationData":[OSD([sQuery(id+"F2.wireOp",EDGE,"E4.bottom")])]})]});
            var Q7;
            Q7=makeQuery(id+"F3.boolean.opBoolean","INTERSECT",EDGE,{"disambiguationData":[OD(1.0)],"derivedFrom":[makeQuery(id+"F1.opExtrude","SWEPT_FACE",FACE,{"disambiguationData":[OSD([sQuery(id+"F0.wireOp",EDGE,"E0")])]}),makeQuery(id+"F3.opExtrude","SWEPT_FACE",FACE,{"disambiguationData":[OSD([sQuery(id+"F2.wireOp",EDGE,"E2.bottom")])]})]});
            var Q8;
            Q8=makeQuery(id+"F3.boolean.opBoolean","INTERSECT",EDGE,{"disambiguationData":[OD(1.0)],"derivedFrom":[makeQuery(id+"F1.opExtrude","SWEPT_FACE",FACE,{"disambiguationData":[OSD([sQuery(id+"F0.wireOp",EDGE,"E0")])]}),makeQuery(id+"F3.opExtrude","SWEPT_FACE",FACE,{"disambiguationData":[OSD([sQuery(id+"F2.wireOp",EDGE,"E2.right")])]})]});
            var Q9;
            {var subQ0=makeQuery(id+"F1.opExtrude","SWEPT_FACE",FACE,{"disambiguationData":[OSD([sQuery(id+"F0.wireOp",EDGE,"E0")])]});Q9=makeQuery(id+"F17.opChamfer","BLEND_EDGE",EDGE,{"blendedFrom":[makeQuery(id+"F3.boolean.opBoolean","INTERSECT",EDGE,{"disambiguationData":[OD(1.0)],"derivedFrom":[subQ0,makeQuery(id+"F3.opExtrude","SWEPT_FACE",FACE,{"disambiguationData":[OSD([sQuery(id+"F2.wireOp",EDGE,"E1.right")])]})]}),subQ0],"blendedInto":[subQ0]});}
            var Q10;
            {var subQ0=makeQuery(id+"F3.opExtrude","SWEPT_FACE",FACE,{"disambiguationData":[OSD([sQuery(id+"F2.wireOp",EDGE,"E1.bottom")])]});Q10=makeQuery(id+"F17.opChamfer","BLEND_EDGE",EDGE,{"blendedFrom":[makeQuery(id+"F3.boolean.opBoolean","INTERSECT",EDGE,{"disambiguationData":[OD(1.0)],"derivedFrom":[makeQuery(id+"F1.opExtrude","SWEPT_FACE",FACE,{"disambiguationData":[OSD([sQuery(id+"F0.wireOp",EDGE,"E0")])]}),subQ0]}),makeQuery(id+"F3.boolean.opBoolean","COPY",FACE,{"derivedFrom":subQ0})],"blendedInto":[makeQuery(id+"F3.boolean.opBoolean","COPY",FACE,{"derivedFrom":subQ0})]});}
            var Q11;
            Q11=makeQuery(id+"F3.boolean.opBoolean","INTERSECT",EDGE,{"disambiguationData":[OD(1.0)],"derivedFrom":[makeQuery(id+"F1.opExtrude","SWEPT_FACE",FACE,{"disambiguationData":[OSD([sQuery(id+"F0.wireOp",EDGE,"E0")])]}),makeQuery(id+"F3.opExtrude","SWEPT_FACE",FACE,{"disambiguationData":[OSD([sQuery(id+"F2.wireOp",EDGE,"E3.right")])]})]});
            var Q12;
            {var subQ0=makeQuery(id+"F1.opExtrude","SWEPT_FACE",FACE,{"disambiguationData":[OSD([sQuery(id+"F0.wireOp",EDGE,"E0")])]});Q12=makeQuery(id+"F17.opChamfer","BLEND_EDGE",EDGE,{"blendedFrom":[makeQuery(id+"F3.boolean.opBoolean","INTERSECT",EDGE,{"disambiguationData":[OD(1.0)],"derivedFrom":[subQ0,makeQuery(id+"F3.opExtrude","SWEPT_FACE",FACE,{"disambiguationData":[OSD([sQuery(id+"F2.wireOp",EDGE,"E4.right")])]})]}),subQ0],"blendedInto":[subQ0]});}
            var Q13;
            Q13=makeQuery(id+"F9.boolean.opBoolean","COPY",EDGE,{"derivedFrom":makeQuery(id+"F9.opExtrude","SWEPT_EDGE",EDGE,{"disambiguationData":[OSD([sQuery(id+"F8.wireOp",EDGE,"E12.top"),sQuery(id+"F8.wireOp",EDGE,"E12.left")])]})});
            var Q14;
            Q14=makeQuery(id+"F9.boolean.opBoolean","INTERSECT",EDGE,{"disambiguationData":[OD(1.0)],"derivedFrom":[makeQuery(id+"F1.opExtrude","SWEPT_FACE",FACE,{"disambiguationData":[OSD([sQuery(id+"F0.wireOp",EDGE,"E0")])]}),makeQuery(id+"F9.opExtrude","SWEPT_FACE",FACE,{"disambiguationData":[OSD([sQuery(id+"F8.wireOp",EDGE,"E12.left")])]})]});
            var Q15;
            Q15=makeQuery(id+"F9.boolean.opBoolean","INTERSECT",EDGE,{"disambiguationData":[OD(1.0)],"derivedFrom":[makeQuery(id+"F1.opExtrude","SWEPT_FACE",FACE,{"disambiguationData":[OSD([sQuery(id+"F0.wireOp",EDGE,"E0")])]}),makeQuery(id+"F9.opExtrude","SWEPT_FACE",FACE,{"disambiguationData":[OSD([sQuery(id+"F8.wireOp",EDGE,"E13.left")])]})]});
            var Q16;
            Q16=makeQuery(id+"F9.boolean.opBoolean","COPY",EDGE,{"derivedFrom":makeQuery(id+"F9.opExtrude","SWEPT_EDGE",EDGE,{"disambiguationData":[OSD([sQuery(id+"F8.wireOp",EDGE,"E13.top"),sQuery(id+"F8.wireOp",EDGE,"E13.left")])]})});
            var Q17;
            Q17=makeQuery(id+"F5.boolean.opBoolean","INTERSECT",EDGE,{"disambiguationData":[OD(2.0)],"derivedFrom":[makeQuery(id+"F1.opExtrude","SWEPT_FACE",FACE,{"disambiguationData":[OSD([sQuery(id+"F0.wireOp",EDGE,"E0")])]}),makeQuery(id+"F5.opExtrude","SWEPT_FACE",FACE,{"disambiguationData":[OSD([sQuery(id+"F4.wireOp",EDGE,"E6.bottom")])]})]});
            var Q18;
            Q18=makeQuery(id+"F7.boolean.opBoolean","INTERSECT",EDGE,{"disambiguationData":[OD(0.0)],"derivedFrom":[makeQuery(id+"F1.opExtrude","SWEPT_FACE",FACE,{"disambiguationData":[OSD([sQuery(id+"F0.wireOp",EDGE,"E0")])]}),makeQuery(id+"F7.opExtrude","SWEPT_FACE",FACE,{"disambiguationData":[OSD([sQuery(id+"F6.wireOp",EDGE,"E7.bottom")])]})]});
            var Q19;
            Q19=makeQuery(id+"F7.boolean.opBoolean","INTERSECT",EDGE,{"disambiguationData":[OD(0.0)],"derivedFrom":[makeQuery(id+"F1.opExtrude","SWEPT_FACE",FACE,{"disambiguationData":[OSD([sQuery(id+"F0.wireOp",EDGE,"E0")])]}),makeQuery(id+"F7.opExtrude","SWEPT_FACE",FACE,{"disambiguationData":[OSD([sQuery(id+"F6.wireOp",EDGE,"E7.top")])]})]});
            var Q20;
            Q20=makeQuery(id+"F7.boolean.opBoolean","INTERSECT",EDGE,{"disambiguationData":[OD(0.0)],"derivedFrom":[makeQuery(id+"F1.opExtrude","SWEPT_FACE",FACE,{"disambiguationData":[OSD([sQuery(id+"F0.wireOp",EDGE,"E0")])]}),makeQuery(id+"F7.opExtrude","SWEPT_FACE",FACE,{"disambiguationData":[OSD([sQuery(id+"F6.wireOp",EDGE,"E8.bottom")])]})]});
            var Q21;
            Q21=makeQuery(id+"F7.boolean.opBoolean","INTERSECT",EDGE,{"disambiguationData":[OD(0.0)],"derivedFrom":[makeQuery(id+"F1.opExtrude","SWEPT_FACE",FACE,{"disambiguationData":[OSD([sQuery(id+"F0.wireOp",EDGE,"E0")])]}),makeQuery(id+"F7.opExtrude","SWEPT_FACE",FACE,{"disambiguationData":[OSD([sQuery(id+"F6.wireOp",EDGE,"E11.bottom")])]})]});
            var Q22;
            Q22=makeQuery(id+"F7.boolean.opBoolean","INTERSECT",EDGE,{"disambiguationData":[OD(0.0)],"derivedFrom":[makeQuery(id+"F1.opExtrude","SWEPT_FACE",FACE,{"disambiguationData":[OSD([sQuery(id+"F0.wireOp",EDGE,"E0")])]}),makeQuery(id+"F7.opExtrude","SWEPT_FACE",FACE,{"disambiguationData":[OSD([sQuery(id+"F6.wireOp",EDGE,"E10.top")])]})]});
            var Q23;
            {var subQ0=makeQuery(id+"F7.opExtrude","SWEPT_FACE",FACE,{"disambiguationData":[OSD([sQuery(id+"F6.wireOp",EDGE,"E10.bottom")])]});Q23=makeQuery(id+"F17.opChamfer","BLEND_EDGE",EDGE,{"blendedFrom":[makeQuery(id+"F7.boolean.opBoolean","INTERSECT",EDGE,{"disambiguationData":[OD(0.0)],"derivedFrom":[makeQuery(id+"F1.opExtrude","SWEPT_FACE",FACE,{"disambiguationData":[OSD([sQuery(id+"F0.wireOp",EDGE,"E0")])]}),subQ0]}),makeQuery(id+"F7.boolean.opBoolean","COPY",FACE,{"derivedFrom":subQ0})],"blendedInto":[makeQuery(id+"F7.boolean.opBoolean","COPY",FACE,{"derivedFrom":subQ0})]});}
            var Q24;
            Q24=makeQuery(id+"F7.boolean.opBoolean","INTERSECT",EDGE,{"disambiguationData":[OD(0.0)],"derivedFrom":[makeQuery(id+"F1.opExtrude","SWEPT_FACE",FACE,{"disambiguationData":[OSD([sQuery(id+"F0.wireOp",EDGE,"E0")])]}),makeQuery(id+"F7.opExtrude","SWEPT_FACE",FACE,{"disambiguationData":[OSD([sQuery(id+"F6.wireOp",EDGE,"E9.top")])]})]});
            var Q25;
            {var subQ0=makeQuery(id+"F7.opExtrude","SWEPT_FACE",FACE,{"disambiguationData":[OSD([sQuery(id+"F6.wireOp",EDGE,"E9.bottom")])]});Q25=makeQuery(id+"F17.opChamfer","BLEND_EDGE",EDGE,{"blendedFrom":[makeQuery(id+"F7.boolean.opBoolean","INTERSECT",EDGE,{"disambiguationData":[OD(0.0)],"derivedFrom":[makeQuery(id+"F1.opExtrude","SWEPT_FACE",FACE,{"disambiguationData":[OSD([sQuery(id+"F0.wireOp",EDGE,"E0")])]}),subQ0]}),makeQuery(id+"F7.boolean.opBoolean","COPY",FACE,{"derivedFrom":subQ0})],"blendedInto":[makeQuery(id+"F7.boolean.opBoolean","COPY",FACE,{"derivedFrom":subQ0})]});}
            var Q26;
            Q26=makeQuery(id+"F7.boolean.opBoolean","INTERSECT",EDGE,{"disambiguationData":[OD(0.0)],"derivedFrom":[makeQuery(id+"F1.opExtrude","SWEPT_FACE",FACE,{"disambiguationData":[OSD([sQuery(id+"F0.wireOp",EDGE,"E0")])]}),makeQuery(id+"F7.opExtrude","SWEPT_FACE",FACE,{"disambiguationData":[OSD([sQuery(id+"F6.wireOp",EDGE,"E8.top")])]})]});
            var Q27;
            Q27=makeQuery(id+"F7.boolean.opBoolean","INTERSECT",EDGE,{"disambiguationData":[OD(0.0)],"derivedFrom":[makeQuery(id+"F1.opExtrude","SWEPT_FACE",FACE,{"disambiguationData":[OSD([sQuery(id+"F0.wireOp",EDGE,"E0")])]}),makeQuery(id+"F7.opExtrude","SWEPT_FACE",FACE,{"disambiguationData":[OSD([sQuery(id+"F6.wireOp",EDGE,"E7.right")])]})]});
            var Q28;
            Q28=makeQuery(id+"F7.boolean.opBoolean","INTERSECT",EDGE,{"disambiguationData":[OD(0.0)],"derivedFrom":[makeQuery(id+"F1.opExtrude","SWEPT_FACE",FACE,{"disambiguationData":[OSD([sQuery(id+"F0.wireOp",EDGE,"E0")])]}),makeQuery(id+"F7.opExtrude","SWEPT_FACE",FACE,{"disambiguationData":[OSD([sQuery(id+"F6.wireOp",EDGE,"E11.top")])]})]});
            chamfer(context, id + "F18", {"entities" : qUnion([Q0, Q1, Q2, Q3, Q4, Q5, Q6, Q7, Q8, Q9, Q10, Q11, Q12, Q13, Q14, Q15, Q16, Q17, Q18, Q19, Q20, Q21, Q22, Q23, Q24, Q25, Q26, Q27, Q28]), "width" : 0.2 * mm, "tangentPropagation" : true});
        }
    });
